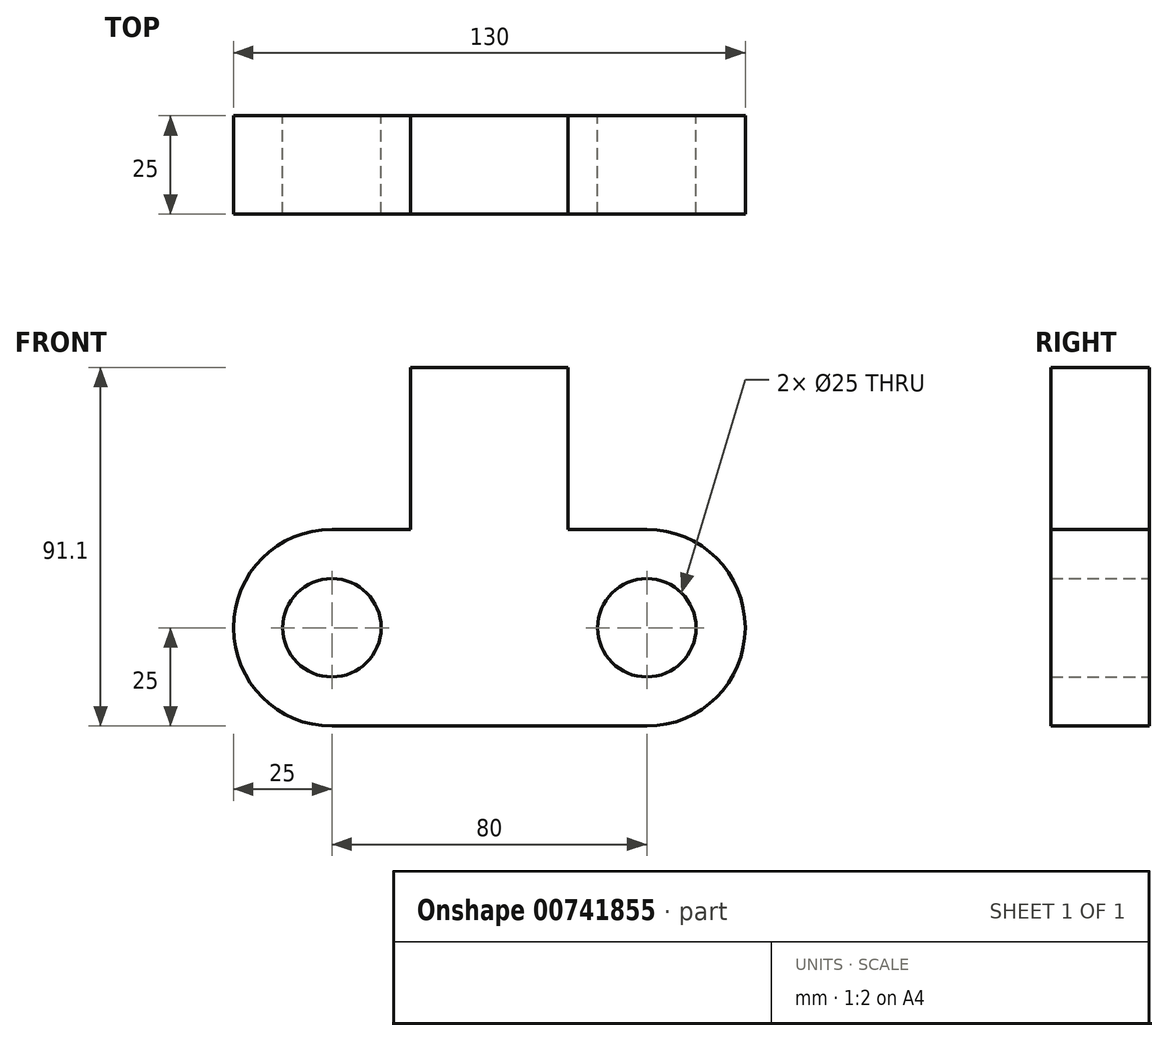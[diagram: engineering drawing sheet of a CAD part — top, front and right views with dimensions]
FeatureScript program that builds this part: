
annotation { "Feature Type Name" : "Feature", "Feature Type Description" : "" }
export const myFeature = defineFeature(function(context is Context, id is Id, definition is map)
    precondition{}
    {
        {
            var Q0;
            Q0=qCreatedBy(makeId("Front.planeOp"),FACE);
            var sketch = newSketch(context, id + "F0", { "sketchPlane" : qUnion([Q0])});
            skArc(sketch, "E0", {"start": v(0, 50) * mm, "mid": v(-25, 25) * mm, "end": v(0, 0) * mm});
            skLineSegment(sketch, "E1.left", {"start": v(0, 50) * mm, "end": v(0, 50) * mm});
            skLineSegment(sketch, "E2.bottom", {"start": v(0, 50) * mm, "end": v(80, 50) * mm});
            skLineSegment(sketch, "E2.top", {"start": v(0, 0) * mm, "end": v(80, 0) * mm});
            skLineSegment(sketch, "E2.left", {"start": v(0, 50) * mm, "end": v(0, 0) * mm});
            skLineSegment(sketch, "E2.right", {"start": v(80, 50) * mm, "end": v(80, 0) * mm});
            skArc(sketch, "E3", {"start": v(80, 0) * mm, "mid": v(105, 25) * mm, "end": v(80, 50) * mm});
            skLineSegment(sketch, "E4", {"start": v(20, 50) * mm, "end": v(20, 0) * mm});
            skLineSegment(sketch, "E5", {"start": v(60, 50) * mm, "end": v(60, 0) * mm});
            skCircle(sketch, "E6", {"center": v(0, 25) * mm, "radius": 12.5 * mm});
            skCircle(sketch, "E7", {"center": v(80, 25) * mm, "radius": 12.5 * mm});
            skLineSegment(sketch, "E8", {"start": v(60, 50) * mm, "end": v(60, 91.1) * mm});
            skLineSegment(sketch, "E9", {"start": v(20, 50) * mm, "end": v(20, 91.1) * mm});
            skLineSegment(sketch, "E10", {"start": v(20, 91.1) * mm, "end": v(60, 91.1) * mm});
            skSolve(sketch);
        }
        {
            var Q0;
            Q0 = qSketchRegion(id + "F0", true);
            extrude(context, id + "F1", {"entities" : qUnion([Q0]), "depth" : 25 * mm, "offsetDistance" : 25 * mm});
        }
    });
